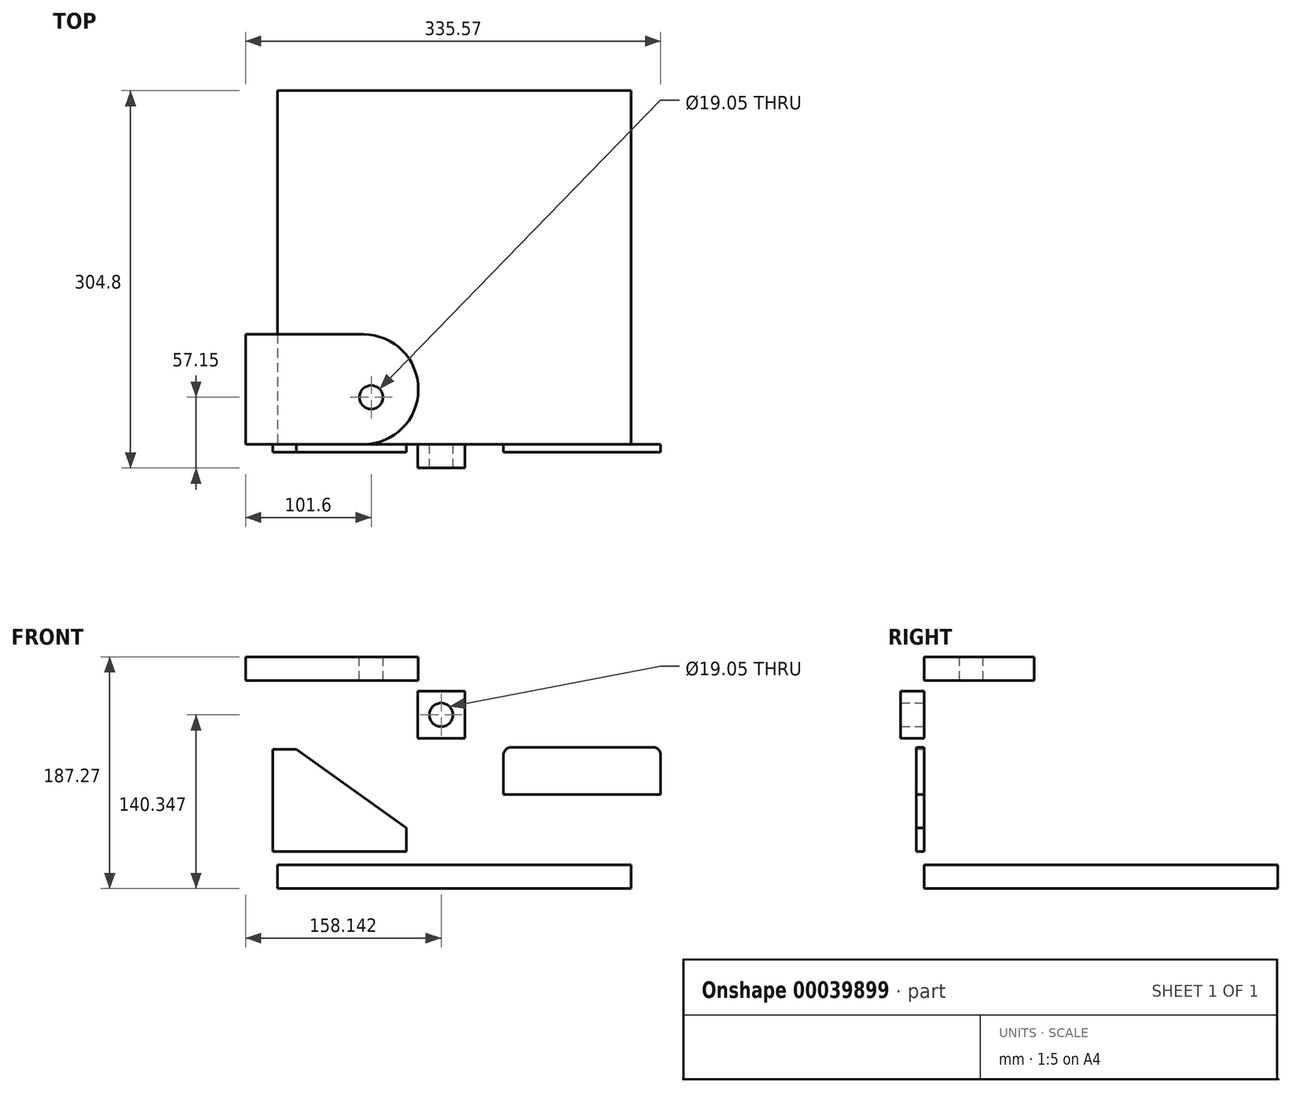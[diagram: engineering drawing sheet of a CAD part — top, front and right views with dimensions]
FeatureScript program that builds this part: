
annotation { "Feature Type Name" : "Feature", "Feature Type Description" : "" }
export const myFeature = defineFeature(function(context is Context, id is Id, definition is map)
    precondition{}
    {
        {
            var Q0;
            Q0=qCreatedBy(makeId("Front.planeOp"),FACE);
            var sketch = newSketch(context, id + "F0", { "sketchPlane" : qUnion([Q0])});
            skLineSegment(sketch, "E0", {"start": v(-47.81, 36.5) * mm, "end": v(-47.81, -46.05) * mm});
            skLineSegment(sketch, "E1", {"start": v(-47.81, -46.05) * mm, "end": v(60.14, -46.05) * mm});
            skLineSegment(sketch, "E2", {"start": v(60.14, -46.05) * mm, "end": v(60.14, -27) * mm});
            skLineSegment(sketch, "E3", {"start": v(-47.81, 36.5) * mm, "end": v(-28.76, 36.5) * mm});
            skLineSegment(sketch, "E4", {"start": v(-28.76, 36.5) * mm, "end": v(60.14, -27) * mm});
            skLineSegment(sketch, "E5.bottom", {"start": v(138.72, 0) * mm, "end": v(265.72, 0) * mm});
            skLineSegment(sketch, "E5.top", {"start": v(138.72, 38.1) * mm, "end": v(265.72, 38.1) * mm});
            skLineSegment(sketch, "E5.left", {"start": v(138.72, 0) * mm, "end": v(138.72, 38.1) * mm});
            skLineSegment(sketch, "E5.right", {"start": v(265.72, 0) * mm, "end": v(265.72, 38.1) * mm});
            skSolve(sketch);
        }
        {
            var Q0;
            Q0=makeQuery(id+"F0.imprint","IMPRINT",FACE,{"disambiguationData":[TD([[makeQuery(id+"F0.imprint","IMPRINT",EDGE,{"derivedFrom":sQuery(id+"F0.wireOp",EDGE,"E0")}),1.0]])]});
            var Q1;
            Q1=makeQuery(id+"F0.imprint","IMPRINT",FACE,{"disambiguationData":[TD([[makeQuery(id+"F0.imprint","IMPRINT",EDGE,{"derivedFrom":sQuery(id+"F0.wireOp",EDGE,"E5.bottom")}),1.0]])]});
            extrude(context, id + "F1", {"entities" : qUnion([Q0, Q1]), "depth" : 6.35 * mm});
        }
        {
            var Q0;
            Q0=makeQuery(id+"F1.opExtrude","SWEPT_EDGE",EDGE,{"disambiguationData":[OSD([sQuery(id+"F0.wireOp",EDGE,"E5.top"),sQuery(id+"F0.wireOp",EDGE,"E5.left")])]});
            var Q1;
            Q1=makeQuery(id+"F1.opExtrude","SWEPT_EDGE",EDGE,{"disambiguationData":[OSD([sQuery(id+"F0.wireOp",EDGE,"E5.top"),sQuery(id+"F0.wireOp",EDGE,"E5.right")])]});
            fillet(context, id + "F2", {"entities" : qUnion([Q0, Q1]), "radius" : 6.35 * mm, "tangentPropagation" : true, "allowEdgeOverflow" : false});
        }
        {
            var Q0;
            Q0=qCreatedBy(makeId("Front.planeOp"),FACE);
            var sketch = newSketch(context, id + "F3", { "sketchPlane" : qUnion([Q0])});
            skLineSegment(sketch, "E6.bottom", {"start": v(-43.96, -57.1) * mm, "end": v(241.79, -57.1) * mm});
            skLineSegment(sketch, "E6.top", {"start": v(-43.96, -76.15) * mm, "end": v(241.79, -76.15) * mm});
            skLineSegment(sketch, "E6.left", {"start": v(-43.96, -57.1) * mm, "end": v(-43.96, -76.15) * mm});
            skLineSegment(sketch, "E6.right", {"start": v(241.79, -57.1) * mm, "end": v(241.79, -76.15) * mm});
            skSolve(sketch);
        }
        {
            var Q0;
            Q0=makeQuery(id+"F3.imprint","IMPRINT",FACE,{"disambiguationData":[TD([[makeQuery(id+"F3.imprint","IMPRINT",EDGE,{"derivedFrom":sQuery(id+"F3.wireOp",EDGE,"E6.bottom")}),-1.0]])]});
            extrude(context, id + "F4", {"entities" : qUnion([Q0]), "oppositeDirection" : true, "depth" : 285.75 * mm});
        }
        {
            var Q0;
            Q0=qCreatedBy(makeId("Front.planeOp"),FACE);
            var sketch = newSketch(context, id + "F5", { "sketchPlane" : qUnion([Q0])});
            skLineSegment(sketch, "E7.rect.bottom", {"start": v(107.34, 83.25) * mm, "end": v(69.24, 83.25) * mm});
            skLineSegment(sketch, "E7.rect.top", {"start": v(107.34, 45.15) * mm, "end": v(69.24, 45.15) * mm});
            skLineSegment(sketch, "E7.rect.left", {"start": v(107.34, 83.25) * mm, "end": v(107.34, 45.15) * mm});
            skLineSegment(sketch, "E7.rect.right", {"start": v(69.24, 83.25) * mm, "end": v(69.24, 45.15) * mm});
            skPoint(sketch, "E7.rect.middle", {"position": v(88.3, 64.2) * mm});
            skCircle(sketch, "E8", {"center": v(88.3, 64.2) * mm, "radius": 9.53 * mm});
            skSolve(sketch);
        }
        {
            var Q0;
            Q0=makeQuery(id+"F5.imprint","IMPRINT",FACE,{"disambiguationData":[TD([[makeQuery(id+"F5.imprint","IMPRINT",EDGE,{"derivedFrom":sQuery(id+"F5.wireOp",EDGE,"E7.rect.bottom")}),1.0]])]});
            extrude(context, id + "F6", {"entities" : qUnion([Q0]), "depth" : 19.05 * mm});
        }
        {
            var Q0;
            Q0=qCreatedBy(makeId("Front.planeOp"),FACE);
            var sketch = newSketch(context, id + "F7", { "sketchPlane" : qUnion([Q0])});
            skLineSegment(sketch, "E9.rect.bottom", {"start": v(69.85, 111.12) * mm, "end": v(-69.85, 111.12) * mm});
            skLineSegment(sketch, "E9.rect.top", {"start": v(69.85, 92.07) * mm, "end": v(-69.85, 92.07) * mm});
            skLineSegment(sketch, "E9.rect.left", {"start": v(69.85, 111.12) * mm, "end": v(69.85, 92.07) * mm});
            skLineSegment(sketch, "E9.rect.right", {"start": v(-69.85, 111.12) * mm, "end": v(-69.85, 92.07) * mm});
            skPoint(sketch, "E9.rect.middle", {"position": v(0, 101.6) * mm});
            skSolve(sketch);
        }
        {
            var Q0;
            Q0=makeQuery(id+"F7.imprint","IMPRINT",FACE,{"disambiguationData":[TD([[makeQuery(id+"F7.imprint","IMPRINT",EDGE,{"derivedFrom":sQuery(id+"F7.wireOp",EDGE,"E9.rect.bottom")}),1.0]])]});
            extrude(context, id + "F8", {"entities" : qUnion([Q0]), "oppositeDirection" : true, "depth" : 88.9 * mm});
        }
        {
            var Q0;
            Q0=makeQuery(id+"F8.opExtrude","SWEPT_FACE",FACE,{"disambiguationData":[OSD([sQuery(id+"F7.wireOp",EDGE,"E9.rect.bottom")])]});
            var sketch = newSketch(context, id + "F9", { "sketchPlane" : qUnion([Q0])});
            skCircle(sketch, "E10", {"center": v(31.75, 38.1) * mm, "radius": 9.53 * mm});
            skSolve(sketch);
        }
        {
            var Q0;
            Q0=makeQuery(id+"F9.imprint","IMPRINT",FACE,{"disambiguationData":[TD([[makeQuery(id+"F9.imprint","IMPRINT",EDGE,{"derivedFrom":sQuery(id+"F9.wireOp",EDGE,"E10")}),1.0]])]});
            extrude(context, id + "F10", {"entities" : qUnion([Q0]), "operationType" : NewBodyOperationType.REMOVE, "oppositeDirection" : true, "depth" : 50.8 * mm});
        }
        {
            var Q0;
            Q0=makeQuery(id+"F8.opExtrude","CAP_EDGE",EDGE,{"disambiguationData":[OSD([sQuery(id+"F7.wireOp",EDGE,"E9.rect.left")])],"isStart":true});
            var Q1;
            Q1=makeQuery(id+"F8.opExtrude","CAP_EDGE",EDGE,{"disambiguationData":[OSD([sQuery(id+"F7.wireOp",EDGE,"E9.rect.left")])],"isStart":false});
            fillet(context, id + "F11", {"entities" : qUnion([Q0, Q1]), "radius" : 44.45 * mm, "tangentPropagation" : true, "allowEdgeOverflow" : false});
        }
    });
